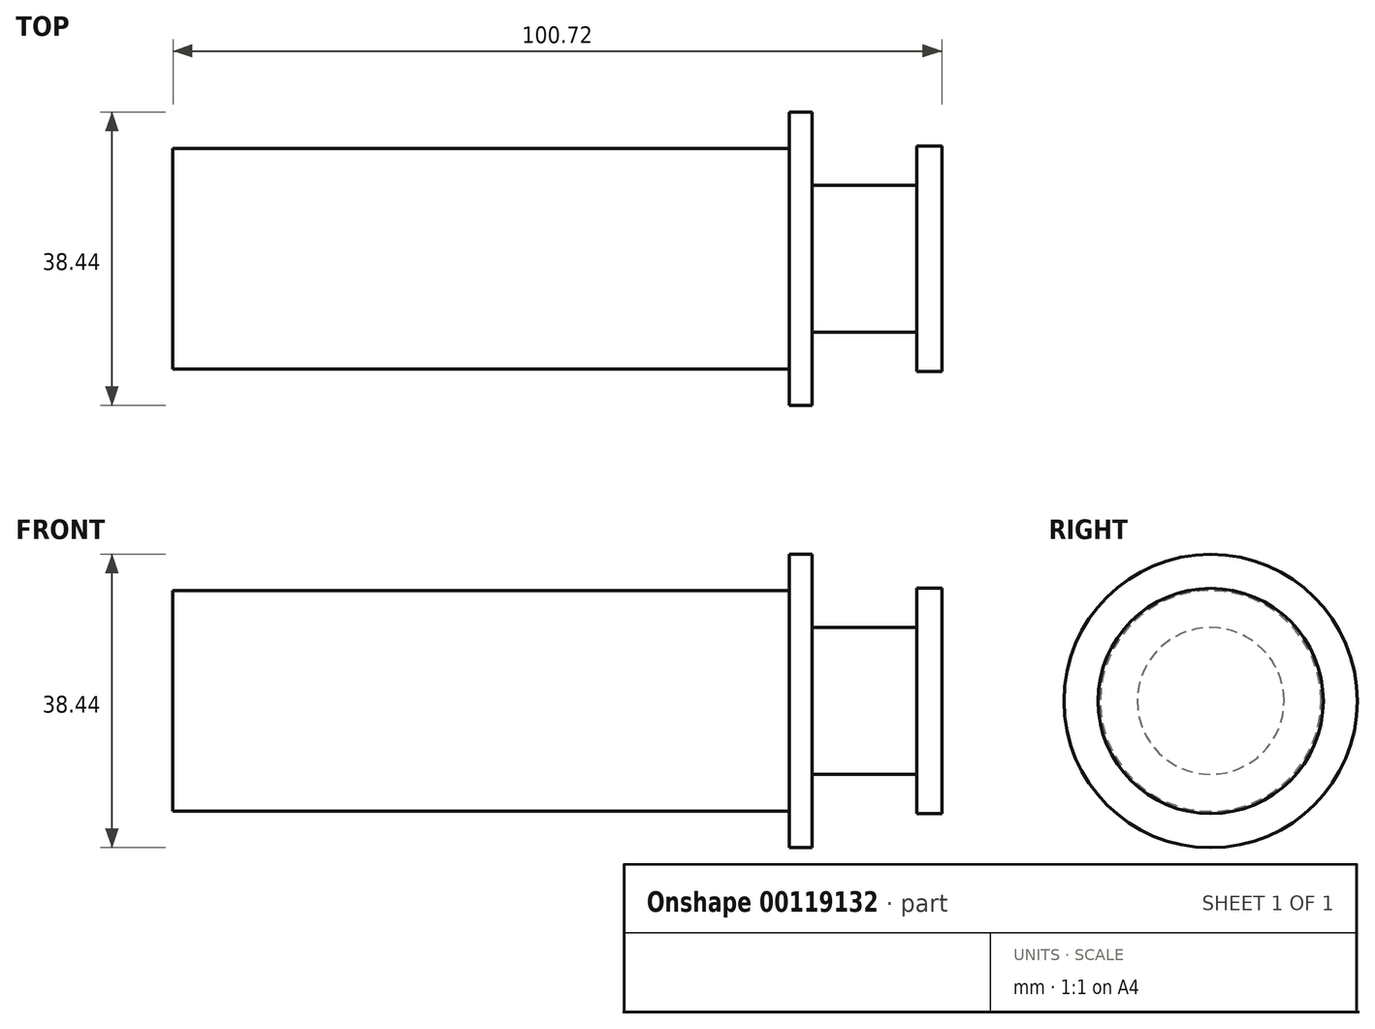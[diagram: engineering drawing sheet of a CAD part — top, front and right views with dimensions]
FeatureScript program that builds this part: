
annotation { "Feature Type Name" : "Feature", "Feature Type Description" : "" }
export const myFeature = defineFeature(function(context is Context, id is Id, definition is map)
    precondition{}
    {
        {
            var Q0;
            Q0=qCreatedBy(makeId("Front.planeOp"),FACE);
            var sketch = newSketch(context, id + "F0", { "sketchPlane" : qUnion([Q0])});
            skLineSegment(sketch, "E0.bottom", {"start": v(-51.25, 0) * mm, "end": v(29.5, 0) * mm});
            skLineSegment(sketch, "E0.top", {"start": v(-51.25, -14.45) * mm, "end": v(29.5, -14.45) * mm});
            skLineSegment(sketch, "E0.left", {"start": v(-51.25, 0) * mm, "end": v(-51.25, -14.45) * mm});
            skLineSegment(sketch, "E0.right", {"start": v(29.5, 0) * mm, "end": v(29.5, -14.45) * mm});
            skLineSegment(sketch, "E1.bottom", {"start": v(29.5, 0) * mm, "end": v(32.48, 0) * mm});
            skLineSegment(sketch, "E1.top", {"start": v(29.5, -19.22) * mm, "end": v(32.48, -19.22) * mm});
            skLineSegment(sketch, "E1.left", {"start": v(29.5, 0) * mm, "end": v(29.5, -19.22) * mm});
            skLineSegment(sketch, "E1.right", {"start": v(32.48, 0) * mm, "end": v(32.48, -19.22) * mm});
            skPoint(sketch, "E2.oppositeSnap0", {"position": v(32.48, -9.61) * mm});
            skLineSegment(sketch, "E2.bottom", {"start": v(32.48, 0) * mm, "end": v(46.19, 0) * mm});
            skLineSegment(sketch, "E2.top", {"start": v(32.48, -9.61) * mm, "end": v(46.19, -9.61) * mm});
            skLineSegment(sketch, "E2.left", {"start": v(32.48, 0) * mm, "end": v(32.48, -9.61) * mm});
            skLineSegment(sketch, "E2.right", {"start": v(46.19, 0) * mm, "end": v(46.19, -9.61) * mm});
            skLineSegment(sketch, "E3.bottom", {"start": v(46.19, 0) * mm, "end": v(49.47, 0) * mm});
            skLineSegment(sketch, "E3.top", {"start": v(46.19, -14.75) * mm, "end": v(49.47, -14.75) * mm});
            skLineSegment(sketch, "E3.left", {"start": v(46.19, 0) * mm, "end": v(46.19, -14.75) * mm});
            skLineSegment(sketch, "E3.right", {"start": v(49.47, 0) * mm, "end": v(49.47, -14.75) * mm});
            skSolve(sketch);
        }
        {
            var Q0;
            Q0 = qSketchRegion(id + "F0", true);
            var Q1;
            Q1=sQuery(id+"F0.wireOp",EDGE,"E0.bottom");
            revolve(context, id + "F1", {"entities" : qUnion([Q0]), "axis" : qUnion([Q1]), "revolveType" : RevolveType.FULL});
        }
    });
